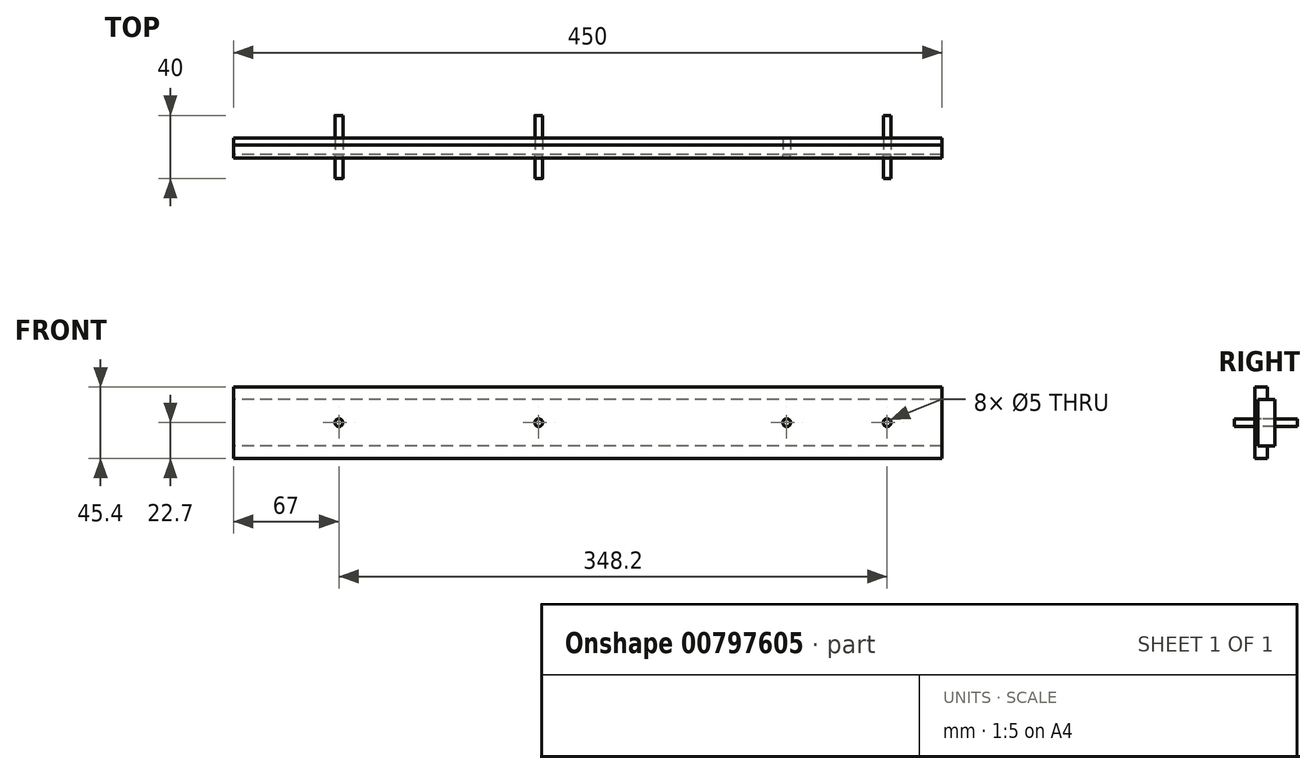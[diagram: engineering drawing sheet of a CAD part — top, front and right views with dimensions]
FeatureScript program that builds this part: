
annotation { "Feature Type Name" : "Feature", "Feature Type Description" : "" }
export const myFeature = defineFeature(function(context is Context, id is Id, definition is map)
    precondition{}
    {
        {
            var Q0;
            Q0=qCreatedBy(makeId("Front.planeOp"),FACE);
            var sketch = newSketch(context, id + "F0", { "sketchPlane" : qUnion([Q0])});
            skLineSegment(sketch, "E0.bottom", {"start": v(-450, 22.7) * mm, "end": v(0, 22.7) * mm});
            skLineSegment(sketch, "E0.top", {"start": v(-450, -22.7) * mm, "end": v(0, -22.7) * mm});
            skLineSegment(sketch, "E0.left", {"start": v(-450, 22.7) * mm, "end": v(-450, -22.7) * mm});
            skLineSegment(sketch, "E0.right", {"start": v(0, 22.7) * mm, "end": v(0, -22.7) * mm});
            skLineSegment(sketch, "E1", {"start": v(-450, 0) * mm, "end": v(0, 0) * mm, "construction": true});
            skCircle(sketch, "E2", {"center": v(-34.8, 0) * mm, "radius": 2.5 * mm});
            skCircle(sketch, "E3", {"center": v(-98.6, 0) * mm, "radius": 2.5 * mm});
            skCircle(sketch, "E4", {"center": v(-256.1, 0) * mm, "radius": 2.5 * mm});
            skCircle(sketch, "E5", {"center": v(-383, 0) * mm, "radius": 2.5 * mm});
            skSolve(sketch);
        }
        {
            var Q0;
            Q0=makeQuery(id+"F0.imprint","IMPRINT",FACE,{"disambiguationData":[TD([[makeQuery(id+"F0.imprint","IMPRINT",EDGE,{"derivedFrom":sQuery(id+"F0.wireOp",EDGE,"E0.bottom")}),-1.0]])]});
            extrude(context, id + "F1", {"entities" : qUnion([Q0]), "depth" : 8 * mm, "offsetDistance" : 25 * mm});
        }
        {
            var Q0;
            Q0=makeQuery(id+"F1.opExtrude","CAP_FACE",FACE,{"disambiguationData":[OSD([sQuery(id+"F0.wireOp",EDGE,"E0.bottom"),sQuery(id+"F0.wireOp",EDGE,"E0.top"),sQuery(id+"F0.wireOp",EDGE,"E0.left"),sQuery(id+"F0.wireOp",EDGE,"E0.right"),sQuery(id+"F0.wireOp",EDGE,"E2"),sQuery(id+"F0.wireOp",EDGE,"E3"),sQuery(id+"F0.wireOp",EDGE,"E4"),sQuery(id+"F0.wireOp",EDGE,"E5")])],"isStart":true});
            var sketch = newSketch(context, id + "F2", { "sketchPlane" : qUnion([Q0])});
            skLineSegment(sketch, "E6.bottom", {"start": v(0, 14.7) * mm, "end": v(450, 14.7) * mm});
            skLineSegment(sketch, "E6.top", {"start": v(0, -14.7) * mm, "end": v(450, -14.7) * mm});
            skLineSegment(sketch, "E6.left", {"start": v(0, 14.7) * mm, "end": v(0, -14.7) * mm});
            skLineSegment(sketch, "E6.right", {"start": v(450, 14.7) * mm, "end": v(450, -14.7) * mm});
            skLineSegment(sketch, "E7", {"start": v(225, 22.7) * mm, "end": v(225, 14.7) * mm, "construction": true});
            skLineSegment(sketch, "E8", {"start": v(225, 14.7) * mm, "end": v(225, -14.7) * mm, "construction": true});
            skLineSegment(sketch, "E9", {"start": v(225, -14.7) * mm, "end": v(225, -22.7) * mm, "construction": true});
            skSolve(sketch);
        }
        {
            var Q0;
            Q0 = qSketchRegion(id + "F2", true);
            extrude(context, id + "F3", {"entities" : qUnion([Q0]), "operationType" : NewBodyOperationType.REMOVE, "oppositeDirection" : true, "depth" : 6 * mm, "offsetDistance" : 25 * mm});
        }
        {
            var Q0;
            Q0=makeQuery(id+"F3.boolean.opBoolean","COPY",FACE,{"derivedFrom":makeQuery(id+"F3.opExtrude","CAP_FACE",FACE,{"disambiguationData":[OSD([sQuery(id+"F2.wireOp",EDGE,"E6.bottom"),sQuery(id+"F2.wireOp",EDGE,"E6.top"),sQuery(id+"F2.wireOp",EDGE,"E6.left"),sQuery(id+"F2.wireOp",EDGE,"E6.right")])],"isStart":false})});
            extrude(context, id + "F4", {"entities" : qUnion([Q0]), "depth" : 10.7 * mm, "offsetDistance" : 25 * mm});
        }
        {
            var Q0;
            Q0=makeQuery(id+"F3.boolean.opBoolean","COPY",FACE,{"derivedFrom":makeQuery(id+"F3.opExtrude","CAP_FACE",FACE,{"disambiguationData":[OSD([sQuery(id+"F2.wireOp",EDGE,"E6.bottom"),sQuery(id+"F2.wireOp",EDGE,"E6.top"),sQuery(id+"F2.wireOp",EDGE,"E6.left"),sQuery(id+"F2.wireOp",EDGE,"E6.right")])],"isStart":false})});
            cPlane(context, id + "F5", {"entities" : qUnion([Q0]), "cplaneType" : CPlaneType.OFFSET, "offset" : 0 * mm, "width" : 150 * mm, "height" : 150 * mm});
        }
        {
            var Q0;
            Q0=qCreatedBy(id+"F5.planeOp",FACE);
            var Q1;
            Q1=qCreatedBy(id+"F5.planeOp",FACE);
            var sketch = newSketch(context, id + "F6", { "sketchPlane" : qUnion([Q0, Q1])});
            skCircle(sketch, "E10.0", {"center": v(34.8, 0) * mm, "radius": 2.5 * mm});
            skCircle(sketch, "E11.0", {"center": v(256.1, 0) * mm, "radius": 2.5 * mm});
            skCircle(sketch, "E12.0", {"center": v(383, 0) * mm, "radius": 2.5 * mm});
            skSolve(sketch);
        }
        {
            var Q0;
            Q0=makeQuery(id+"F6.imprint","IMPRINT",FACE,{"disambiguationData":[TD([[makeQuery(id+"F6.imprint","IMPRINT",EDGE,{"derivedFrom":sQuery(id+"F6.wireOp",EDGE,"E10.0")}),1.0]])]});
            var Q1;
            Q1=makeQuery(id+"F6.imprint","IMPRINT",FACE,{"disambiguationData":[TD([[makeQuery(id+"F6.imprint","IMPRINT",EDGE,{"derivedFrom":sQuery(id+"F6.wireOp",EDGE,"E11.0")}),1.0]])]});
            var Q2;
            Q2=makeQuery(id+"F6.imprint","IMPRINT",FACE,{"disambiguationData":[TD([[makeQuery(id+"F6.imprint","IMPRINT",EDGE,{"derivedFrom":sQuery(id+"F6.wireOp",EDGE,"E12.0")}),1.0]])]});
            extrude(context, id + "F7", {"entities" : qUnion([Q0, Q1, Q2]), "depth" : 25 * mm, "offsetDistance" : 25 * mm});
        }
        {
            var Q0;
            Q0=makeQuery(id+"F7.opExtrude","CAP_FACE",FACE,{"disambiguationData":[OSD([sQuery(id+"F6.wireOp",EDGE,"E10.0")])],"isStart":true});
            var Q1;
            Q1=makeQuery(id+"F7.opExtrude","CAP_FACE",FACE,{"disambiguationData":[OSD([sQuery(id+"F6.wireOp",EDGE,"E11.0")])],"isStart":true});
            var Q2;
            Q2=makeQuery(id+"F7.opExtrude","CAP_FACE",FACE,{"disambiguationData":[OSD([sQuery(id+"F6.wireOp",EDGE,"E12.0")])],"isStart":true});
            extrude(context, id + "F8", {"entities" : qUnion([Q0, Q1, Q2]), "depth" : 15 * mm, "offsetDistance" : 25 * mm});
        }
    });
